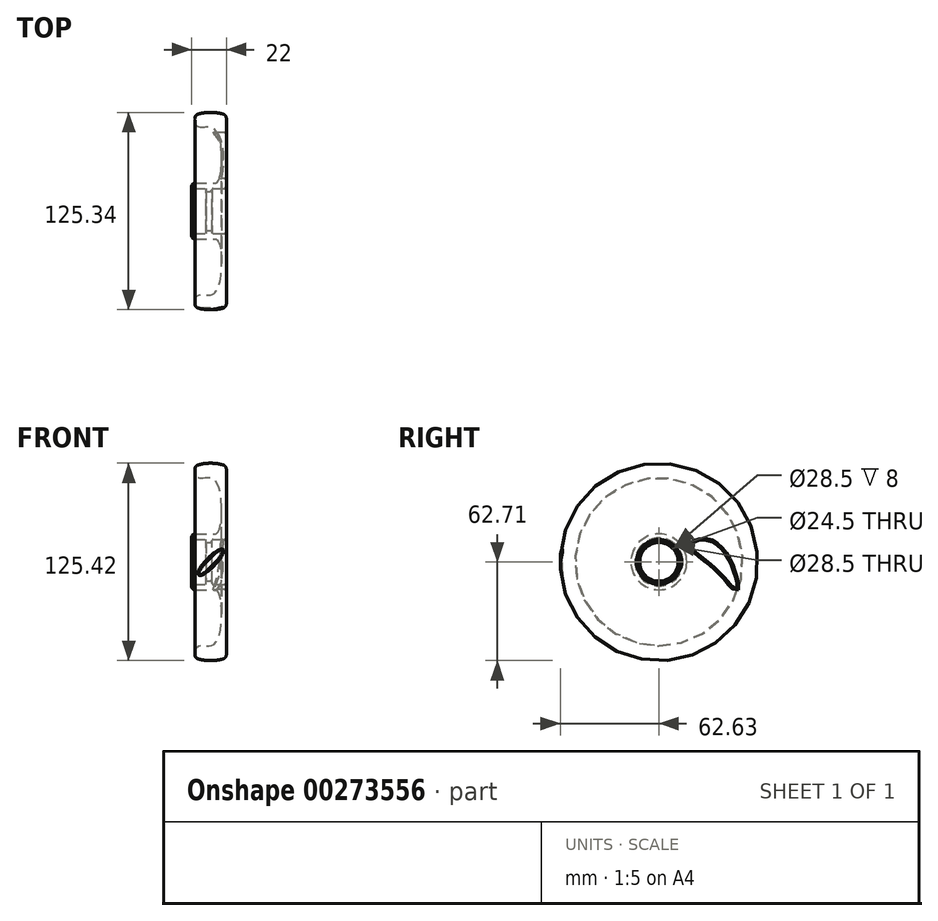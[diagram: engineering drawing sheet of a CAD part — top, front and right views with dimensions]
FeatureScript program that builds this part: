
annotation { "Feature Type Name" : "Feature", "Feature Type Description" : "" }
export const myFeature = defineFeature(function(context is Context, id is Id, definition is map)
    precondition{}
    {
        {
            var Q0;
            Q0=qCreatedBy(makeId("Front.planeOp"),FACE);
            var sketch = newSketch(context, id + "F0", { "sketchPlane" : qUnion([Q0])});
            skLineSegment(sketch, "E0", {"start": v(0, 0) * mm, "end": v(-22, 0) * mm});
            skLineSegment(sketch, "E1", {"start": v(-22, 0) * mm, "end": v(-22, 17.75) * mm});
            skLineSegment(sketch, "E2", {"start": v(-22, 17.75) * mm, "end": v(-6.98, 17.75) * mm});
            skLineSegment(sketch, "E3", {"start": v(0, 0) * mm, "end": v(0, 61) * mm});
            skFitSpline(sketch, "E4", {"points": [v(-20, 58.83) * mm, v(-8.07, 52.54) * mm, v(-6.98, 17.75) * mm], "startDerivative": vector(0, -78.06) * mm, "endDerivative": vector(-24.6, 0) * mm});
            skLineSegment(sketch, "E5", {"start": v(-9, 0) * mm, "end": v(-9, 14.25) * mm});
            skLineSegment(sketch, "E6", {"start": v(-9, 14.25) * mm, "end": v(0, 14.25) * mm});
            skLineSegment(sketch, "E7", {"start": v(-22, 14.25) * mm, "end": v(-13, 14.25) * mm});
            skLineSegment(sketch, "E8", {"start": v(-13, 14.25) * mm, "end": v(-13, 0) * mm});
            skLineSegment(sketch, "E9", {"start": v(-13, 12.25) * mm, "end": v(-9, 12.25) * mm});
            skPoint(sketch, "E10", {"position": v(-6.48, 62.5) * mm});
            skLineSegment(sketch, "E11", {"start": v(-20, 61) * mm, "end": v(-20, 58.83) * mm});
            skArc(sketch, "E12.trimOffspring", {"start": v(0, 61) * mm, "mid": v(-10, 62.7) * mm, "end": v(-20, 61) * mm});
            skPoint(sketch, "E13", {"position": v(-3, 34.94) * mm});
            skSolve(sketch);
        }
        {
            var Q0;
            {var subQ5=sQuery(id+"F0.wireOp",EDGE,"E2");Q0=makeQuery(id+"F0.imprint","IMPRINT",FACE,{"disambiguationData":[TD([[makeQuery(id+"F0.imprint","IMPRINT",EDGE,{"derivedFrom":subQ5}),-1.0]])]});}
            var Q1;
            {var subQ0=sQuery(id+"F0.wireOp",EDGE,"HNAj4O2R-bTQW-l742-k01n-k4t6RiFG52qu");Q1=makeQuery(id+"F0.imprint","IMPRINT",FACE,{"disambiguationData":[TD([[makeQuery(id+"F0.imprint","IMPRINT",EDGE,{"derivedFrom":subQ0}),1.0]])]});}
            var Q2;
            {var subQ0=sQuery(id+"F0.wireOp",EDGE,"HNAj4O2R-bTQW-l742-k01n-k4t6RiFG52qu");Q2=makeQuery(id+"F0.imprint","IMPRINT",FACE,{"disambiguationData":[TD([[makeQuery(id+"F0.imprint","IMPRINT",EDGE,{"derivedFrom":subQ0}),-1.0]])]});}
            var Q3;
            Q3=sQuery(id+"F0.wireOp",EDGE,"E0");
            revolve(context, id + "F1", {"entities" : qUnion([Q0, Q1, Q2]), "axis" : qUnion([Q3]), "revolveType" : RevolveType.FULL});
        }
        {
            var Q0;
            Q0=makeQuery(id+"F1.opRevolve","SWEPT_EDGE",EDGE,{"disambiguationData":[OSD([sQuery(id+"F0.wireOp",EDGE,"E1"),sQuery(id+"F0.wireOp",EDGE,"E2")])]});
            fillet(context, id + "F2", {"entities" : qUnion([Q0]), "radius" : 2 * mm, "tangentPropagation" : true, "allowEdgeOverflow" : false});
        }
        {
            var Q0;
            Q0=makeQuery(id+"F1.opRevolve","SWEPT_EDGE",EDGE,{"disambiguationData":[OSD([sQuery(id+"F0.wireOp",EDGE,"E5"),sQuery(id+"F0.wireOp",EDGE,"E9")])]});
            chamfer(context, id + "F3", {"entities" : qUnion([Q0]), "width" : 1 * mm, "tangentPropagation" : true});
        }
        {
            var Q0;
            Q0=makeQuery(id+"F1.opRevolve","SWEPT_EDGE",EDGE,{"disambiguationData":[OSD([sQuery(id+"F0.wireOp",EDGE,"E5"),sQuery(id+"F0.wireOp",EDGE,"E6")])]});
            fillet(context, id + "F4", {"entities" : qUnion([Q0]), "radius" : .5 * mm, "tangentPropagation" : true, "allowEdgeOverflow" : false});
        }
        {
            var Q0;
            Q0=makeQuery(id+"F1.opRevolve","SWEPT_EDGE",EDGE,{"disambiguationData":[OSD([sQuery(id+"F0.wireOp",EDGE,"E3"),sQuery(id+"F0.wireOp",EDGE,"E6")])]});
            chamfer(context, id + "F5", {"entities" : qUnion([Q0]), "width" : 1 * mm, "tangentPropagation" : true});
        }
        {
            var Q0;
            Q0=makeQuery(id+"F5.opChamfer","BLEND_FACE",FACE,{"disambiguationData":[OSD([sQuery(id+"F0.wireOp",EDGE,"E3"),sQuery(id+"F0.wireOp",EDGE,"E6")])]});
            var Q1;
            Q1=makeQuery(id+"F1.opRevolve","SWEPT_FACE",FACE,{"disambiguationData":[OSD([sQuery(id+"F0.wireOp",EDGE,"E9")])]});
            fillet(context, id + "F6", {"entities" : qUnion([Q0, Q1]), "radius" : .5 * mm, "tangentPropagation" : true, "allowEdgeOverflow" : false});
        }
        {
            var Q0;
            Q0=makeQuery(id+"F1.opRevolve","SWEPT_EDGE",EDGE,{"disambiguationData":[OSD([sQuery(id+"F0.wireOp",EDGE,"E1"),sQuery(id+"F0.wireOp",EDGE,"E7")])]});
            chamfer(context, id + "F7", {"entities" : qUnion([Q0]), "width" : 1 * mm, "tangentPropagation" : true});
        }
        {
            var Q0;
            Q0=makeQuery(id+"F1.opRevolve","SWEPT_FACE",FACE,{"disambiguationData":[OSD([sQuery(id+"F0.wireOp",EDGE,"E12.trimOffspring")])]});
            fillet(context, id + "F8", {"entities" : qUnion([Q0]), "radius" : 3 * mm, "tangentPropagation" : true, "allowEdgeOverflow" : false});
        }
        {
            var Q0;
            Q0=makeQuery(id+"F1.opRevolve","SWEPT_FACE",FACE,{"disambiguationData":[OSD([sQuery(id+"F0.wireOp",EDGE,"E3")])]});
            var sketch = newSketch(context, id + "F9", { "sketchPlane" : qUnion([Q0])});
            skFitSpline(sketch, "E14", {"points": [v(49.58, -17.36) * mm, v(36.4, 11.24) * mm, v(20.8, 10.78) * mm, v(36.62, -4.72) * mm, v(49.58, -17.36) * mm]});
            skSolve(sketch);
        }
        {
            var Q0;
            Q0=makeQuery(id+"F9.imprint","IMPRINT",FACE,{"disambiguationData":[TD([[makeQuery(id+"F9.imprint","IMPRINT",EDGE,{"derivedFrom":sQuery(id+"F9.wireOp",EDGE,"E14")}),1.0]])]});
            extrude(context, id + "F10", {"entities" : qUnion([Q0]), "operationType" : NewBodyOperationType.REMOVE, "endBound" : BoundingType.THROUGH_ALL, "oppositeDirection" : true, "depth" : 25 * mm});
        }
        {
            var Q0;
            Q0=makeQuery(id+"F10.boolean.opBoolean","COPY",FACE,{"derivedFrom":makeQuery(id+"F10.opExtrude","SWEPT_FACE",FACE,{"disambiguationData":[OSD([sQuery(id+"F9.wireOp",EDGE,"E14")])]})});
            fillet(context, id + "F11", {"entities" : qUnion([Q0]), "radius" : 1 * mm, "tangentPropagation" : true, "allowEdgeOverflow" : false});
        }
        {
            var Q0;
            Q0=qCreatedBy(makeId("Right.planeOp"),FACE);
            var sketch = newSketch(context, id + "F12", { "sketchPlane" : qUnion([Q0])});
            skLineSegment(sketch, "E15", {"start": v(0, 0) * mm, "end": v(-75.02, 0) * mm});
            skSolve(sketch);
        }
        {
            var Q0;
            Q0=sQuery(id+"F12.wireOp",EDGE,"E15");
            var Q1;
            Q1=qCreatedBy(makeId("Right.planeOp"),FACE);
            cPlane(context, id + "F13", {"entities" : qUnion([Q0, Q1]), "cplaneType" : CPlaneType.LINE_ANGLE, "offset" : 25 * mm, "angle" : 45 * degree, "width" : 150 * mm, "height" : 150 * mm});
        }
        {
            var Q0;
            Q0=qCreatedBy(id+"F13.planeOp",FACE);
            var sketch = newSketch(context, id + "F14", { "sketchPlane" : qUnion([Q0])});
            skCircle(sketch, "E16", {"center": v(63.89, 6.84) * mm, "radius": 2.72 * mm});
            skSolve(sketch);
        }
        {
            var Q0;
            Q0 = qSketchRegion(id + "F14", true);
            extrude(context, id + "F15", {"entities" : qUnion([Q0]), "operationType" : NewBodyOperationType.REMOVE, "endBound" : BoundingType.THROUGH_ALL, "depth" : 25 * mm, "hasSecondDirection" : true, "secondDirectionBound" : SecondDirectionBoundingType.THROUGH_ALL, "secondDirectionOppositeDirection" : true, "secondDirectionDepth" : 25 * mm});
        }
        {
            var Q0;
            Q0=makeQuery(id+"F15.boolean.opBoolean","INTERSECT",EDGE,{"disambiguationData":[OD(1.0)],"derivedFrom":[makeQuery(id+"F1.opRevolve","SWEPT_FACE",FACE,{"disambiguationData":[OSD([sQuery(id+"F0.wireOp",EDGE,"E12.trimOffspring")])]}),makeQuery(id+"F15.opExtrude","SWEPT_FACE",FACE,{"disambiguationData":[OSD([sQuery(id+"F14.wireOp",EDGE,"E16")])]})]});
            fillet(context, id + "F16", {"entities" : qUnion([Q0]), "radius" : 1 * mm, "tangentPropagation" : true, "allowEdgeOverflow" : false});
        }
    });
